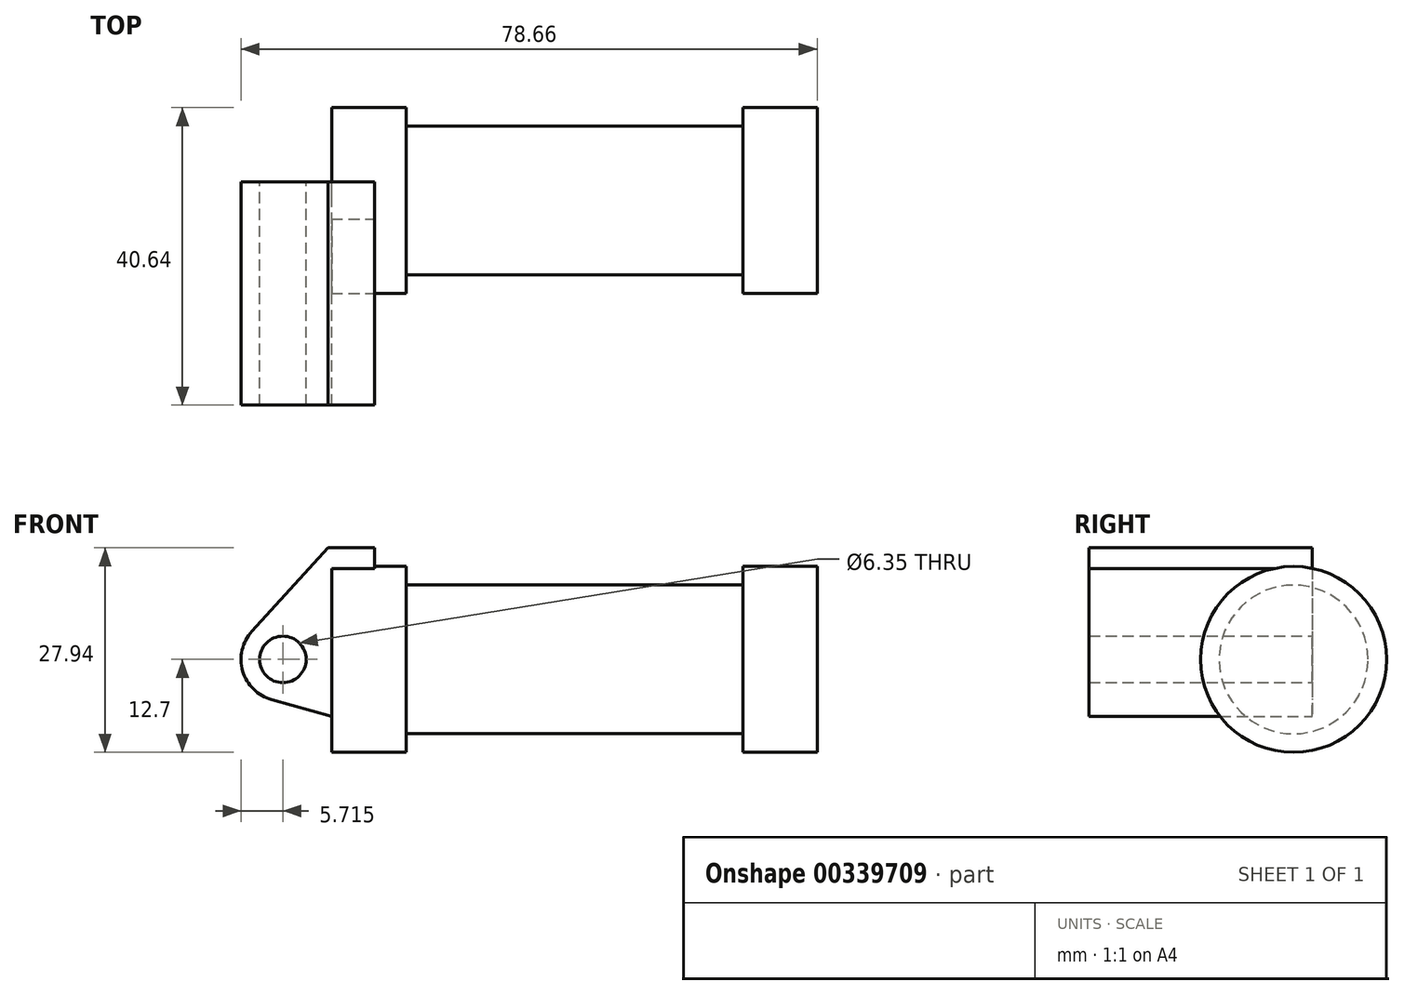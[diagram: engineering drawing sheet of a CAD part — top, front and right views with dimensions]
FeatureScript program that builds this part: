
annotation { "Feature Type Name" : "Feature", "Feature Type Description" : "" }
export const myFeature = defineFeature(function(context is Context, id is Id, definition is map)
    precondition{}
    {
        {
            var Q0;
            Q0=qCreatedBy(makeId("Front.planeOp"),FACE);
            var sketch = newSketch(context, id + "F0", { "sketchPlane" : qUnion([Q0])});
            skLineSegment(sketch, "E0", {"start": v(0, 0) * mm, "end": v(0, 12.7) * mm});
            skLineSegment(sketch, "E1", {"start": v(0, 12.7) * mm, "end": v(10.16, 12.7) * mm});
            skLineSegment(sketch, "E2", {"start": v(10.16, 12.7) * mm, "end": v(10.16, 10.16) * mm});
            skLineSegment(sketch, "E3", {"start": v(10.16, 10.16) * mm, "end": v(56.13, 10.16) * mm});
            skLineSegment(sketch, "E4", {"start": v(56.13, 10.16) * mm, "end": v(56.13, 12.7) * mm});
            skLineSegment(sketch, "E5", {"start": v(56.13, 12.7) * mm, "end": v(66.3, 12.7) * mm});
            skLineSegment(sketch, "E6", {"start": v(66.3, 12.7) * mm, "end": v(66.3, 0) * mm});
            skLineSegment(sketch, "E7", {"start": v(66.3, 0) * mm, "end": v(0, 0) * mm});
            skLineSegment(sketch, "E8", {"start": v(5.84, 15.24) * mm, "end": v(-0.5, 15.24) * mm});
            skLineSegment(sketch, "E9", {"start": v(-0.5, 15.24) * mm, "end": v(-10.88, 3.85) * mm});
            skLineSegment(sketch, "E10", {"start": v(0, 0) * mm, "end": v(-6.65, 0) * mm});
            skCircle(sketch, "E11", {"center": v(-6.65, 0) * mm, "radius": 5.72 * mm});
            skCircle(sketch, "E12", {"center": v(-6.65, 0) * mm, "radius": 3.18 * mm});
            skLineSegment(sketch, "E13", {"start": v(5.84, 15.24) * mm, "end": v(5.84, -9.4) * mm});
            skLineSegment(sketch, "E14", {"start": v(5.84, -9.4) * mm, "end": v(-8.18, -5.5) * mm});
            skSolve(sketch);
        }
        {
            var Q0;
            {var subQ0=sQuery(id+"F0.wireOp",EDGE,"E0");Q0=makeQuery(id+"F0.imprint","IMPRINT",FACE,{"disambiguationData":[TD([[makeQuery(id+"F0.imprint","IMPRINT",EDGE,{"derivedFrom":subQ0}),-1.0]])]});}
            var Q1;
            {var subQ0=sQuery(id+"F0.wireOp",EDGE,"E2");Q1=makeQuery(id+"F0.imprint","IMPRINT",FACE,{"disambiguationData":[TD([[makeQuery(id+"F0.imprint","IMPRINT",EDGE,{"derivedFrom":subQ0}),-1.0]])]});}
            var Q2;
            Q2=sQuery(id+"F0.wireOp",EDGE,"E7");
            revolve(context, id + "F1", {"entities" : qUnion([Q0, Q1]), "axis" : qUnion([Q2]), "revolveType" : RevolveType.FULL});
        }
        {
            var Q0;
            {var subQ0=sQuery(id+"F0.wireOp",EDGE,"E14");Q0=makeQuery(id+"F0.imprint","IMPRINT",FACE,{"disambiguationData":[TD([[makeQuery(id+"F0.imprint","IMPRINT",EDGE,{"derivedFrom":subQ0}),-1.0]])]});}
            var Q1;
            {var subQ5=sQuery(id+"F0.wireOp",EDGE,"E12");Q1=makeQuery(id+"F0.imprint","IMPRINT",FACE,{"disambiguationData":[TD([[makeQuery(id+"F0.imprint","IMPRINT",EDGE,{"derivedFrom":subQ5}),-1.0]])]});}
            extrude(context, id + "F2", {"entities" : qUnion([Q0, Q1]), "operationType" : NewBodyOperationType.ADD, "depth" : 5.08 * mm, "offsetDistance" : 25.4 * mm, "symmetric" : true});
        }
        {
            var Q0;
            {var subQ1=sQuery(id+"F0.wireOp",EDGE,"E0");Q0=makeQuery(id+"F0.imprint","IMPRINT",FACE,{"disambiguationData":[TD([[makeQuery(id+"F0.imprint","IMPRINT",EDGE,{"derivedFrom":subQ1}),1.0]])]});}
            var Q1;
            {var subQ0=sQuery(id+"F0.wireOp",EDGE,"E0");Q1=makeQuery(id+"F0.imprint","IMPRINT",FACE,{"disambiguationData":[TD([[makeQuery(id+"F0.imprint","IMPRINT",EDGE,{"derivedFrom":subQ0}),-1.0]])]});}
            extrude(context, id + "F3", {"entities" : qUnion([Q0, Q1]), "operationType" : NewBodyOperationType.ADD, "depth" : 5.08 * mm, "symmetric" : true});
        }
        {
            var Q0;
            {var subQ0=sQuery(id+"F0.wireOp",EDGE,"E13");var subQ1=sQuery(id+"F0.wireOp",EDGE,"E11");var subQ2=sQuery(id+"F0.wireOp",EDGE,"E10");var subQ3=sQuery(id+"F0.wireOp",EDGE,"E7");Q0=makeQuery(id+"F3.boolean.opBoolean","MERGE",FACE,{"derivedFrom":[makeQuery(id+"F2.opExtrude","CAP_FACE",FACE,{"disambiguationData":[OSD([subQ3,subQ2,subQ1,sQuery(id+"F0.wireOp",EDGE,"E12"),subQ0,sQuery(id+"F0.wireOp",EDGE,"E14")])],"isStart":false}),makeQuery(id+"F3.opExtrude","CAP_FACE",FACE,{"disambiguationData":[OSD([subQ3,sQuery(id+"F0.wireOp",EDGE,"E8"),sQuery(id+"F0.wireOp",EDGE,"E9"),subQ2,subQ1,subQ0])],"isStart":false})]});}
            extrude(context, id + "F4", {"entities" : qUnion([Q0]), "operationType" : NewBodyOperationType.ADD, "depth" : 25.4 * mm, "offsetDistance" : 25.4 * mm});
        }
    });
